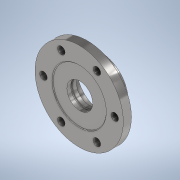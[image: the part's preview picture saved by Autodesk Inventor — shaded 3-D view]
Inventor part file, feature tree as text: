
AUTODESK INVENTOR PART (.ipt)
format: ipt  version: 2020 (Build 240168000, 168)  size: 207,360 bytes
history: native  units: mm
features: extrude x7, sketch x7, plane x3, other x3, reference x2, fillet x1, projected_geometry x1
ambient origin geometry x8: Origin, YZ Plane, XZ Plane, XY Plane, X Axis, Y Axis, Z Axis, Center Point
bodies: 实体1 (feature_tree)
feature tree (24):
  plane  "工作平面1"
  extrude  "拉伸1"  Depth=11.0mm
  extrude  "拉伸2"  Depth=70.0mm
  extrude  "拉伸3"  Depth=12.0mm
  extrude  "拉伸4"  Depth=20.0mm TaperAngle=0.0deg
  fillet  "圆角1"  Radius=30.0mm
  plane  "工作平面2"
  extrude  "拉伸5"  Depth=1.0mm TaperAngle=0.0deg
  extrude  "拉伸6"  Depth=1.0mm
  plane  "工作平面3"
  extrude  "拉伸7"  Depth=2.65mm
  sketch  "草图1"  dims[d0=105.0mm d1=11.0mm]
  reference  "参考1"
  sketch  "草图2"  dims[d2=60.0mm d4=360.0deg d6=70.0mm]
  sketch  "草图3"  dims[d7=12.0mm d8=0.0mm d9=70.0mm]
  reference  "参考2"
  sketch  "草图4"  dims[d10=80.0mm d11=20.0mm d12=0.0mm d14=30.0mm d15=0.0mm]
  sketch  "草图5"  dims[d16=80.0mm d17=1.0mm d18=0.0mm]
  sketch  "草图6"  dims[d19=1.0mm d20=1.0mm]
  projected_geometry  "投影回路1"
  sketch  "草图7"  dims[d21=2.0mm d22=0.0mm d23=38.0mm d24=3.0mm d25=0.0mm d26=-7.0mm d27=40.8mm d28=2.65mm d29=0.0mm]
  other  "<userpath>\Desktop\ME_course_project\课设试试\shaft_try_1.iam"
  other  "shaft_try_1.iam"
  other  "xia(1):1"
